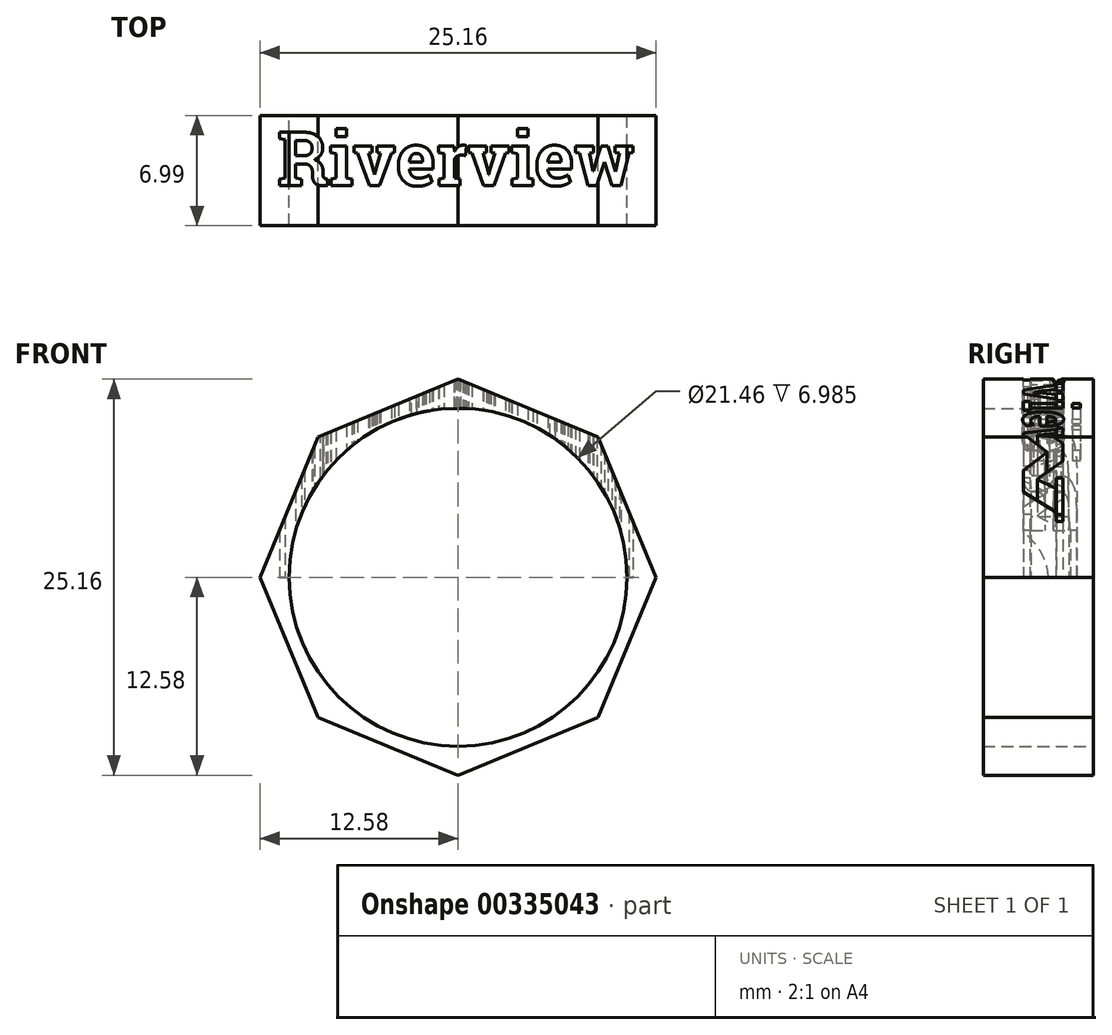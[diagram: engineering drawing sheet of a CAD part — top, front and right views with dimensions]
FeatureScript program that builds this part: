
annotation { "Feature Type Name" : "Feature", "Feature Type Description" : "" }
export const myFeature = defineFeature(function(context is Context, id is Id, definition is map)
    precondition{}
    {
        {
            var Q0;
            Q0=qCreatedBy(makeId("Front.planeOp"),FACE);
            var sketch = newSketch(context, id + "F0", { "sketchPlane" : qUnion([Q0])});
            skCircle(sketch, "E0", {"center": v(0, 0) * mm, "radius": 10.73 * mm});
            skLineSegment(sketch, "E1", {"start": v(0, 0) * mm, "end": v(-13.54, 13.54) * mm});
            skLineSegment(sketch, "E2", {"start": v(0, 0) * mm, "end": v(-13.06, -13.06) * mm});
            skLineSegment(sketch, "E3", {"start": v(-12.58, 0) * mm, "end": v(-8.9, 8.9) * mm});
            skLineSegment(sketch, "E4", {"start": v(-8.9, 8.9) * mm, "end": v(0, 12.58) * mm});
            skLineSegment(sketch, "E5", {"start": v(-12.58, 0) * mm, "end": v(-8.9, -8.9) * mm});
            skLineSegment(sketch, "E6", {"start": v(-8.9, -8.9) * mm, "end": v(0, -12.58) * mm});
            skLineSegment(sketch, "E7.MirrorCS", {"start": v(8.9, 8.9) * mm, "end": v(0, 12.58) * mm});
            skLineSegment(sketch, "E8.MirrorCS", {"start": v(12.58, 0) * mm, "end": v(8.9, 8.9) * mm});
            skLineSegment(sketch, "E9.MirrorCS", {"start": v(12.58, 0) * mm, "end": v(8.9, -8.9) * mm});
            skLineSegment(sketch, "E10.MirrorCS", {"start": v(8.9, -8.9) * mm, "end": v(0, -12.58) * mm});
            skSolve(sketch);
        }
        {
            var Q0;
            Q0 = qSketchRegion(id + "F0", true);
            extrude(context, id + "F1", {"entities" : qUnion([Q0]), "depth" : 7 * mm, "offsetDistance" : 25.4 * mm});
        }
        {
            var Q0;
            Q0=qCreatedBy(makeId("Top.planeOp"),FACE);
            var sketch = newSketch(context, id + "F2", { "sketchPlane" : qUnion([Q0])});
            skText(sketch, "E11", { "text": "Riverview", "fontName": "RobotoSlab-Bold.ttf"});
            const initialGuessF2  = {"E11": [-0.01148, -0.00444, 1, 0, 0.00343]};
            skSetInitialGuess(sketch, initialGuessF2);
            skSolve(sketch);
        }
        {
            var Q0;
            Q0 = qSketchRegion(id + "F2", true);
            extrude(context, id + "F3", {"entities" : qUnion([Q0]), "operationType" : NewBodyOperationType.REMOVE, "depth" : 25.4 * mm});
        }
    });
